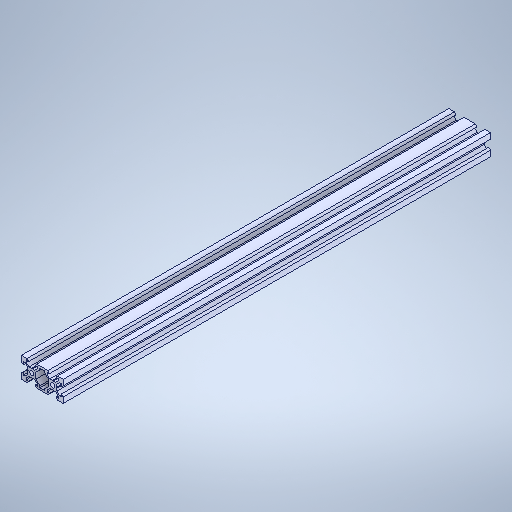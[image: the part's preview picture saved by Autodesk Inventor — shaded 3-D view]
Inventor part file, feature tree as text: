
AUTODESK INVENTOR PART (.ipt)
format: ipt  version: 2025.2 (Build 292293000, 293)  size: 359,936 bytes
history: native  units: in
note: dims shown in document units (in); Inventor stores cm internally (conversion verified against a paired STEP export)
features: extrude x1, sketch x1, other x1
ambient origin geometry x8: Origin, YZ Plane, XZ Plane, XY Plane, X Axis, Y Axis, Z Axis, Center Point
bodies: Solid1 (feature_tree)
feature tree (3):
  extrude  "Extrusion1"  [1 undecoded]
  sketch  "Sketch1"  dims[d0=3.5433in d1=0.0in]
  other  "Boss-Extrude1"
note: 1 required parameter value undecoded (feature->parameter linkage not recoverable at this tier; creation-order binding heuristic only, values carry confidence <= 0.55)
